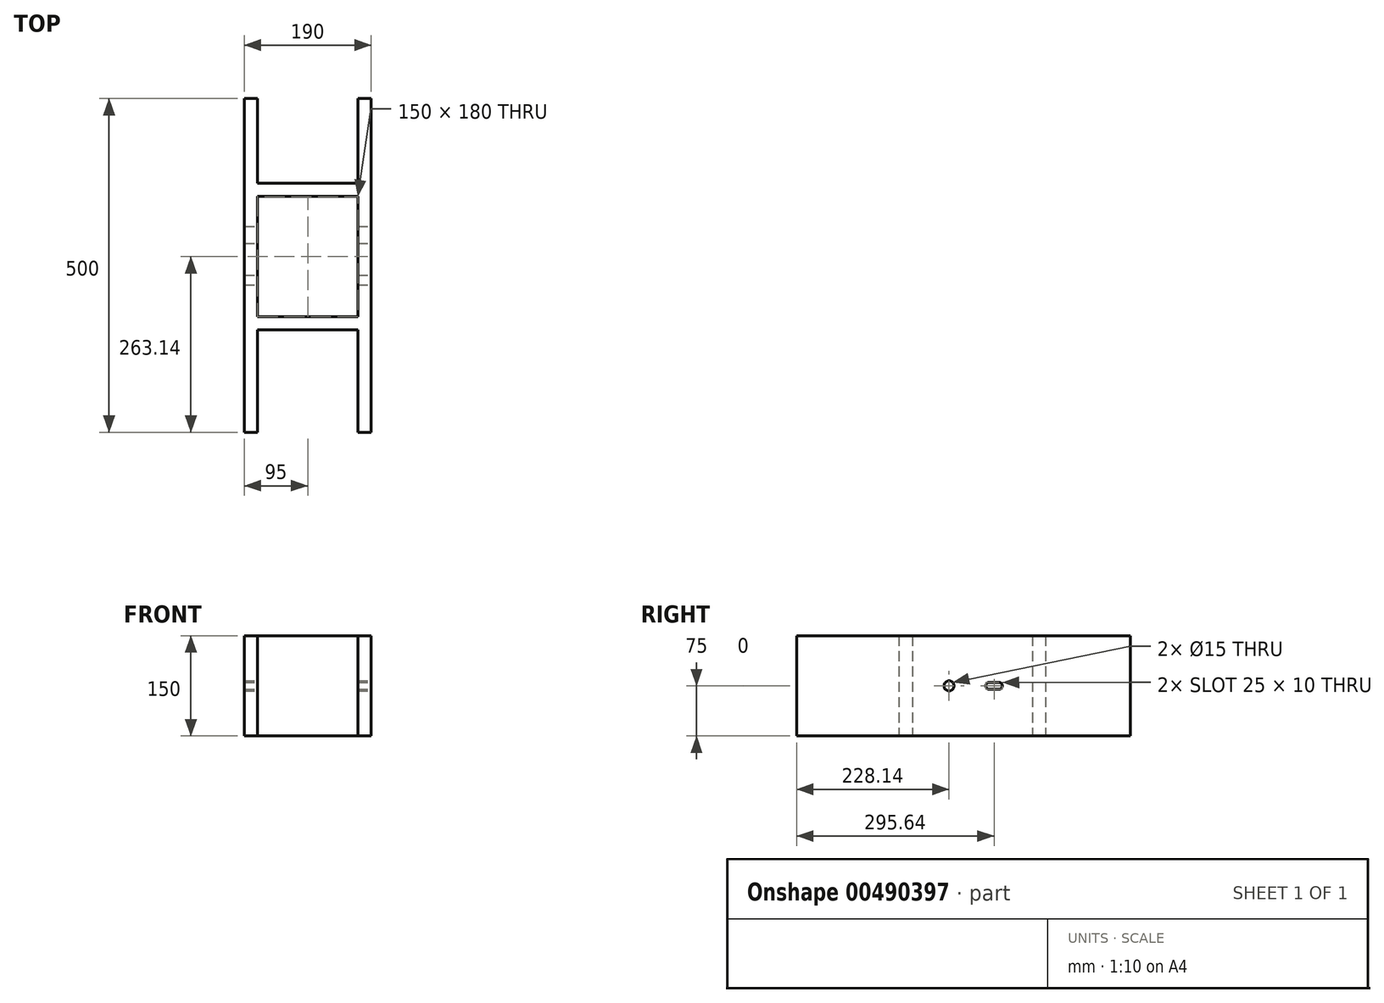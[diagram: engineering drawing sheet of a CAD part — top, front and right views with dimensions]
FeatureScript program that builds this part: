
annotation { "Feature Type Name" : "Feature", "Feature Type Description" : "" }
export const myFeature = defineFeature(function(context is Context, id is Id, definition is map)
    precondition{}
    {
        {
            var Q0;
            Q0=qCreatedBy(makeId("Top.planeOp"),FACE);
            var sketch = newSketch(context, id + "F0", { "sketchPlane" : qUnion([Q0])});
            skLineSegment(sketch, "E0", {"start": v(-75, 236.86) * mm, "end": v(-75, -263.14) * mm});
            skLineSegment(sketch, "E1.MirrorCS", {"start": v(75, 236.86) * mm, "end": v(75, -263.14) * mm});
            skLineSegment(sketch, "E2", {"start": v(-75, 90) * mm, "end": v(75, 90) * mm});
            skLineSegment(sketch, "E3.0", {"start": v(-95, 236.86) * mm, "end": v(-95, -263.14) * mm});
            skLineSegment(sketch, "E4.0", {"start": v(95, 236.86) * mm, "end": v(95, -263.14) * mm});
            skLineSegment(sketch, "E5.0", {"start": v(-150, 110) * mm, "end": v(150, 110) * mm});
            skLineSegment(sketch, "E6.MirrorCS", {"start": v(-75, -90) * mm, "end": v(75, -90) * mm});
            skLineSegment(sketch, "E7.0", {"start": v(-150, -110) * mm, "end": v(150, -110) * mm});
            skLineSegment(sketch, "E8", {"start": v(-95, 236.86) * mm, "end": v(-75, 236.86) * mm});
            skLineSegment(sketch, "E9", {"start": v(75, 236.86) * mm, "end": v(95, 236.86) * mm});
            skLineSegment(sketch, "E10", {"start": v(-95, -263.14) * mm, "end": v(-75, -263.14) * mm});
            skLineSegment(sketch, "E11", {"start": v(75, -263.14) * mm, "end": v(95, -263.14) * mm});
            skSolve(sketch);
        }
        {
            var Q0;
            Q0=makeQuery(id+"F0.imprint","IMPRINT",FACE,{"disambiguationData":[TD([[makeQuery(id+"F0.imprint","IMPRINT",EDGE,{"derivedFrom":sQuery(id+"F0.wireOp",EDGE,"E3.0")}),1.0]])]});
            var Q1;
            {var subQ0=sQuery(id+"F0.wireOp",EDGE,"E2");Q1=makeQuery(id+"F0.imprint","IMPRINT",FACE,{"disambiguationData":[TD([[makeQuery(id+"F0.imprint","IMPRINT",EDGE,{"derivedFrom":subQ0}),1.0]])]});}
            var Q2;
            {var subQ0=sQuery(id+"F0.wireOp",EDGE,"E6.MirrorCS");Q2=makeQuery(id+"F0.imprint","IMPRINT",FACE,{"disambiguationData":[TD([[makeQuery(id+"F0.imprint","IMPRINT",EDGE,{"derivedFrom":subQ0}),-1.0]])]});}
            var Q3;
            Q3=makeQuery(id+"F0.imprint","IMPRINT",FACE,{"disambiguationData":[TD([[makeQuery(id+"F0.imprint","IMPRINT",EDGE,{"derivedFrom":sQuery(id+"F0.wireOp",EDGE,"E4.0")}),-1.0]])]});
            var Q4;
            {var subQ0=sQuery(id+"F0.wireOp",EDGE,"E0");var subQ8=makeQuery(id+"F0.imprint","INTERSECT",VERTEX,{"derivedFrom":[subQ0,sQuery(id+"F0.wireOp",EDGE,"E2")]});Q4=makeQuery(id+"F0.imprint","IMPRINT",FACE,{"disambiguationData":[TD([[makeQuery(id+"F0.imprint","IMPRINT",EDGE,{"disambiguationData":[TD([[subQ8,1.0]])],"derivedFrom":subQ0}),-1.0]])]});}
            var Q5;
            {var subQ5=sQuery(id+"F0.wireOp",EDGE,"E1.MirrorCS");var subQ9=makeQuery(id+"F0.imprint","INTERSECT",VERTEX,{"derivedFrom":[subQ5,sQuery(id+"F0.wireOp",EDGE,"E2")]});Q5=makeQuery(id+"F0.imprint","IMPRINT",FACE,{"disambiguationData":[TD([[makeQuery(id+"F0.imprint","IMPRINT",EDGE,{"disambiguationData":[TD([[subQ9,1.0]])],"derivedFrom":subQ5}),1.0]])]});}
            extrude(context, id + "F1", {"entities" : qUnion([Q0, Q1, Q2, Q3, Q4, Q5]), "depth" : 150 * mm});
        }
        {
            var Q0;
            Q0=makeQuery(id+"F1.opExtrude","SWEPT_FACE",FACE,{"disambiguationData":[OSD([sQuery(id+"F0.wireOp",EDGE,"E4.0")])]});
            var sketch = newSketch(context, id + "F2", { "sketchPlane" : qUnion([Q0])});
            skLineSegment(sketch, "E12", {"start": v(-263.14, 75) * mm, "end": v(236.86, 75) * mm, "construction": true});
            skLineSegment(sketch, "E13", {"start": v(0, 0) * mm, "end": v(0, 150) * mm, "construction": true});
            skCircle(sketch, "E14", {"center": v(-35, 75) * mm, "radius": 7.5 * mm});
            skArc(sketch, "E15", {"start": v(25, 80) * mm, "mid": v(20, 75) * mm, "end": v(25, 70) * mm});
            skArc(sketch, "E16", {"start": v(40, 70) * mm, "mid": v(45, 75) * mm, "end": v(40, 80) * mm});
            skLineSegment(sketch, "E17", {"start": v(25, 80) * mm, "end": v(40, 80) * mm});
            skLineSegment(sketch, "E18", {"start": v(25, 70) * mm, "end": v(40, 70) * mm});
            skSolve(sketch);
        }
        {
            var Q0;
            Q0=makeQuery(id+"F2.imprint","IMPRINT",FACE,{"disambiguationData":[TD([[makeQuery(id+"F2.imprint","IMPRINT",EDGE,{"derivedFrom":sQuery(id+"F2.wireOp",EDGE,"E14")}),1.0]])]});
            var Q1;
            Q1=makeQuery(id+"F2.imprint","IMPRINT",FACE,{"disambiguationData":[TD([[makeQuery(id+"F2.imprint","IMPRINT",EDGE,{"derivedFrom":sQuery(id+"F2.wireOp",EDGE,"E15")}),1.0]])]});
            extrude(context, id + "F3", {"entities" : qUnion([Q0, Q1]), "operationType" : NewBodyOperationType.REMOVE, "oppositeDirection" : true, "depth" : 412 * mm});
        }
    });
